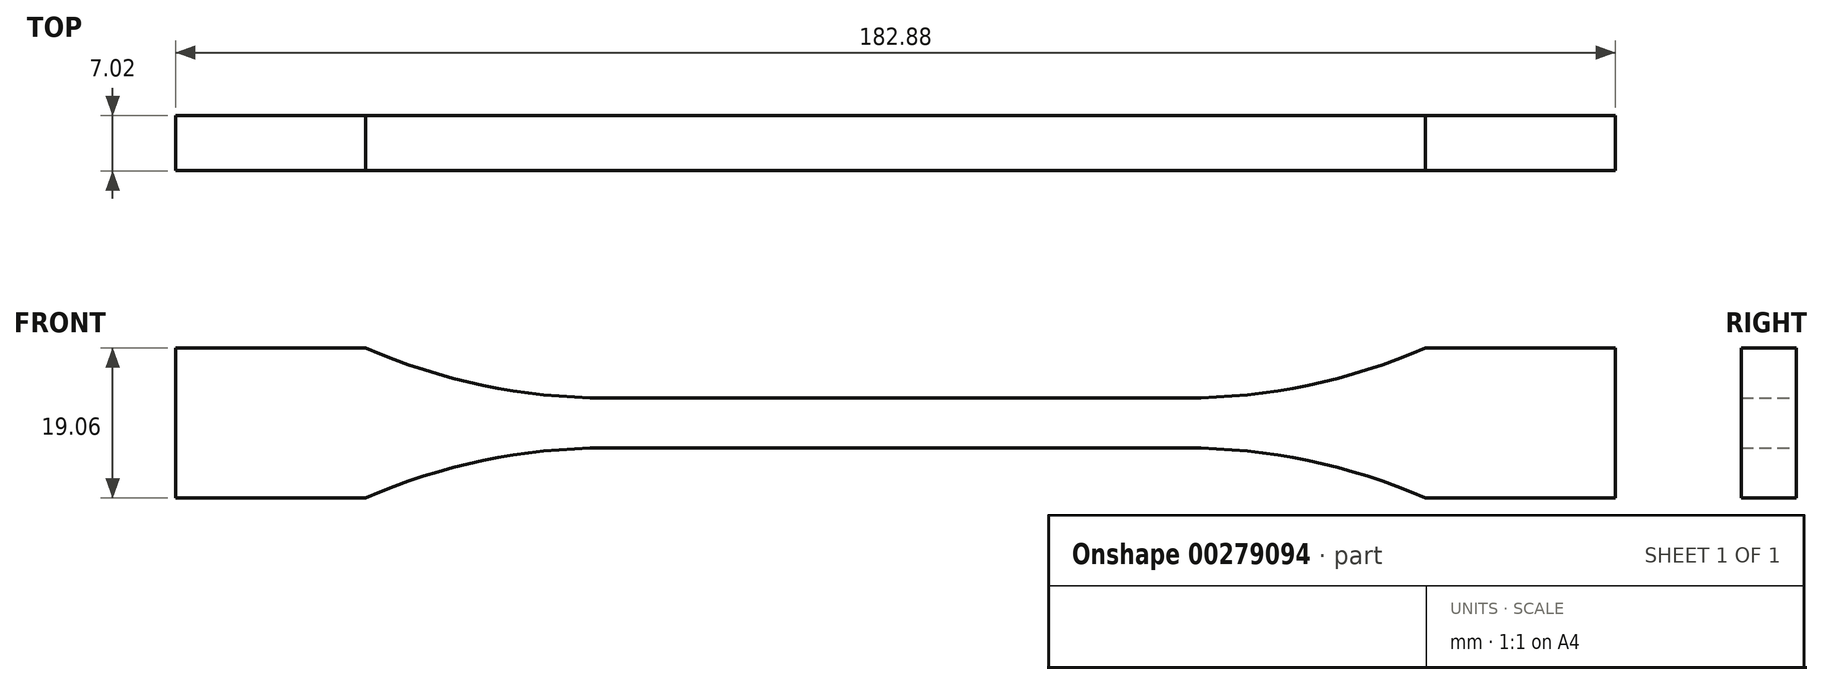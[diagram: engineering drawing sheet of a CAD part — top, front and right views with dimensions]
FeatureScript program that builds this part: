
annotation { "Feature Type Name" : "Feature", "Feature Type Description" : "" }
export const myFeature = defineFeature(function(context is Context, id is Id, definition is map)
    precondition{}
    {
        {
            var Q0;
            Q0=qCreatedBy(makeId("Front.planeOp"),FACE);
            var sketch = newSketch(context, id + "F0", { "sketchPlane" : qUnion([Q0])});
            skLineSegment(sketch, "E0", {"start": v(0, 3.18) * mm, "end": v(36.86, 3.18) * mm});
            skArc(sketch, "E1", {"start": v(36.86, 3.18) * mm, "mid": v(52.41, 4.78) * mm, "end": v(67.31, 9.53) * mm});
            skLineSegment(sketch, "E2", {"start": v(67.31, 9.53) * mm, "end": v(91.44, 9.53) * mm});
            skLineSegment(sketch, "E3.MirrorCS", {"start": v(67.31, -9.53) * mm, "end": v(91.44, -9.53) * mm});
            skLineSegment(sketch, "E4.MirrorCS", {"start": v(0, -3.18) * mm, "end": v(36.86, -3.18) * mm});
            skArc(sketch, "E5.MirrorCS", {"start": v(36.86, -3.18) * mm, "mid": v(52.41, -4.78) * mm, "end": v(67.31, -9.53) * mm});
            skArc(sketch, "E6.MirrorCS", {"start": v(-36.86, -3.18) * mm, "mid": v(-52.41, -4.78) * mm, "end": v(-67.31, -9.53) * mm});
            skLineSegment(sketch, "E7.MirrorCS", {"start": v(0, 3.18) * mm, "end": v(-36.86, 3.17) * mm});
            skArc(sketch, "E8.MirrorCS", {"start": v(-36.86, 3.18) * mm, "mid": v(-52.41, 4.78) * mm, "end": v(-67.31, 9.53) * mm});
            skLineSegment(sketch, "E9.MirrorCS", {"start": v(-67.31, -9.53) * mm, "end": v(-91.44, -9.53) * mm});
            skLineSegment(sketch, "E10.MirrorCS", {"start": v(0, -3.17) * mm, "end": v(-36.86, -3.18) * mm});
            skLineSegment(sketch, "E11.MirrorCS", {"start": v(-67.31, 9.53) * mm, "end": v(-91.44, 9.52) * mm});
            skLineSegment(sketch, "E12", {"start": v(91.44, 9.52) * mm, "end": v(91.44, -9.52) * mm});
            skLineSegment(sketch, "E13", {"start": v(-91.44, 9.52) * mm, "end": v(-91.44, -9.52) * mm});
            skSolve(sketch);
        }
        {
            var Q0;
            Q0=makeQuery(id+"F0.imprint","IMPRINT",FACE,{"disambiguationData":[TD([[makeQuery(id+"F0.imprint","IMPRINT",EDGE,{"derivedFrom":sQuery(id+"F0.wireOp",EDGE,"E0")}),-1.0]])]});
            extrude(context, id + "F1", {"entities" : qUnion([Q0]), "endBound" : BoundingType.SYMMETRIC, "depth" : 7 * mm});
        }
    });
